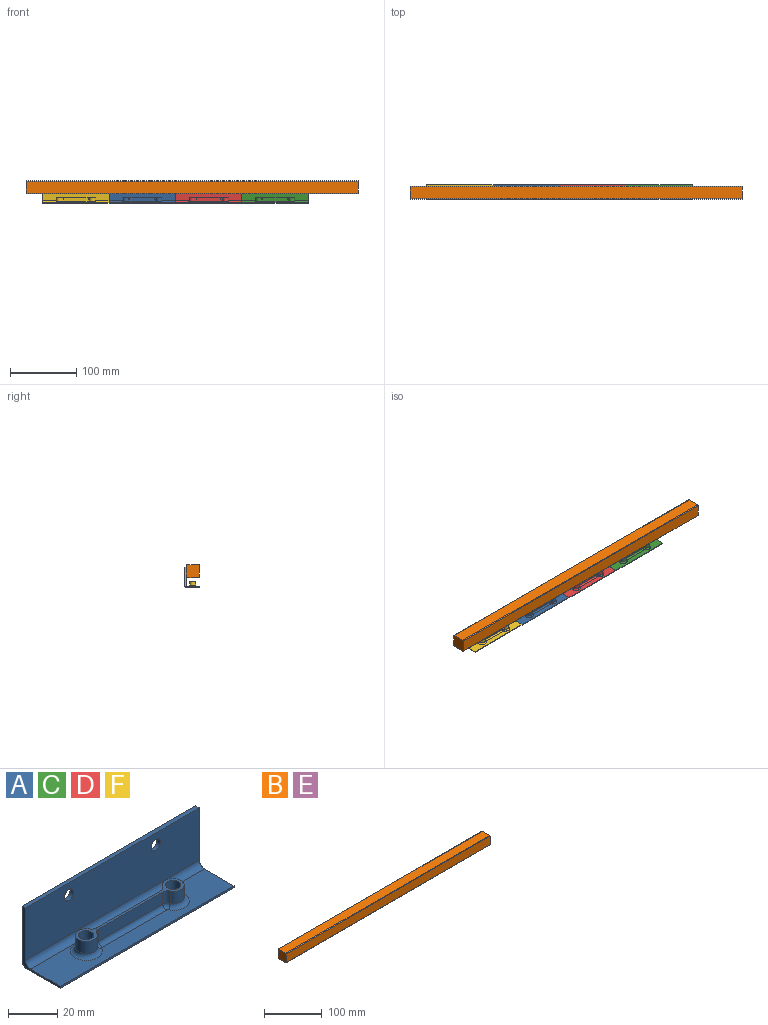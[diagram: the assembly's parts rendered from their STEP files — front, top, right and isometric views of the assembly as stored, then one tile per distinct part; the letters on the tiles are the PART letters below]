
ASSEMBLY  parts=6 mates=4
PART A: 35 faces, bbox 100x22x30 mm
  f0: plane 100x27mm, normal (0,1,0), area 2654.2mm2, adj f4,f5,f16,f20,f33,f34
  f1: plane 100x26mm, normal (0,-1,0), area 2554.2mm2, adj f4,f5,f16,f19,f33,f34
  f2: plane 100x19mm, normal (0,0,-1), area 1885.9mm2, adj f4,f5,f6,f17,f18,f20
  f3: plane 100x17mm, normal (0,0,1), area 1240mm2, adj f4,f5,f6,f19,f25,f26,f27,f28
  f4: plane 30x22mm, normal (1,0,0), area 80mm2, adj f0,f1,f2,f3,f6,f16,f19,f20
  f5: plane 30x22mm, normal (-1,0,0), area 80mm2, adj f0,f1,f2,f3,f6,f16,f19,f20
  f6: plane 100x1mm, normal (0,-1,0), area 100mm2, adj f2,f3,f4,f5
  f7: plane 36.84x6mm, normal (0,1,0), area 221mm2, adj f13,f22,f24,f28
  f8: cylinder r=4.5mm len=9mm, axis (0,0,-1), area 142.6mm2, adj f13,f21,f22,f25
  f9: plane 36.84x6mm, normal (0,-1,0), area 221mm2, adj f13,f21,f23,f29
  f10: cylinder r=3.1mm len=8mm, axis (0,0,-1), area 155.8mm2, adj f13,f14
  f11: cylinder r=4.5mm len=9mm, axis (0,0,-1), area 142.6mm2, adj f13,f23,f24,f32
  f12: cylinder r=3.1mm len=8mm, axis (0,0,-1), area 155.8mm2, adj f13,f15
  f13: plane 59x9mm, normal (0,0,1), area 118.9mm2, adj f7,f8,f9,f10,f11,f12,f21,f22
  f14: plane 6.2x6.2mm, normal (0,0,1), area 23.1mm2, adj f10,f17
  f15: plane 6.2x6.2mm, normal (0,0,1), area 23.1mm2, adj f12,f18
  f16: plane 100x2mm, normal (0,0,1), area 200mm2, adj f0,f1,f4,f5
  f17: cylinder r=1.5mm len=3mm, axis (0,0,1), area 9.4mm2, adj f2,f14
  f18: cylinder r=1.5mm len=3mm, axis (0,0,1), area 9.4mm2, adj f2,f15
  f19: cylinder r=3mm len=100mm, axis (-1,0,0), area 471.2mm2, adj f1,f3,f4,f5
  f20: cylinder r=3mm len=100mm, axis (-1,0,0), area 471.2mm2, adj f0,f2,f4,f5
  f21: cylinder r=3mm len=6mm, axis (0,0,-1), area 19.3mm2, adj f8,f9,f13,f27
  f22: cylinder r=3mm len=6mm, axis (0,0,-1), area 19.3mm2, adj f7,f8,f13,f26
  f23: cylinder r=3mm len=6mm, axis (0,0,-1), area 19.3mm2, adj f9,f11,f13,f31
  f24: cylinder r=3mm len=6mm, axis (0,0,-1), area 19.3mm2, adj f7,f11,f13,f30
  f25: torus R=6.5mm, axis (0,0,1), area 86.7mm2, adj f3,f8,f26,f27
  f26: torus R=1mm, axis (0,0,1), area 7.6mm2, adj f3,f22,f25,f28
  f27: torus R=1mm, axis (0,0,1), area 7.6mm2, adj f3,f21,f25,f29
  f28: cylinder r=2mm len=36.84mm, axis (-1,0,0), area 115.7mm2, adj f3,f7,f26,f30
  f29: cylinder r=2mm len=36.84mm, axis (1,0,0), area 115.7mm2, adj f3,f9,f27,f31
  f30: torus R=1mm, axis (0,0,1), area 7.6mm2, adj f3,f24,f28,f32
  f31: torus R=1mm, axis (0,0,1), area 7.6mm2, adj f3,f23,f29,f32
  f32: torus R=6.5mm, axis (0,0,1), area 86.7mm2, adj f3,f11,f30,f31
  f33: cylinder r=2.7mm len=5.4mm, axis (0,1,0), area 33.9mm2, adj f0,f1
  f34: cylinder r=2.7mm len=5.4mm, axis (0,1,0), area 33.9mm2, adj f0,f1
PART B: 10 faces, bbox 500x20x20 mm
  f0: plane 500x18mm, normal (0,-1,0), area 9000mm2, adj f1,f3,f7,f9
  f1: plane 20x20mm, normal (1,0,0), area 399.1mm2, adj f0,f2,f4,f5,f6,f7,f8,f9
  f2: plane 500x18mm, normal (0,1,0), area 9000mm2, adj f1,f3,f6,f8
  f3: plane 20x20mm, normal (-1,0,0), area 399.1mm2, adj f0,f2,f4,f5,f6,f7,f8,f9
  f4: plane 500x18mm, normal (0,0,1), area 9000mm2, adj f1,f3,f8,f9
  f5: plane 500x18mm, normal (0,0,-1), area 9000mm2, adj f1,f3,f6,f7
  f6: cylinder r=1mm len=500mm, axis (-1,0,0), area 785.4mm2, adj f1,f2,f3,f5
  f7: cylinder r=1mm len=500mm, axis (1,0,0), area 785.4mm2, adj f0,f1,f3,f5
  f8: cylinder r=1mm len=500mm, axis (1,0,0), area 785.4mm2, adj f1,f2,f3,f4
  f9: cylinder r=1mm len=500mm, axis (-1,0,0), area 785.4mm2, adj f0,f1,f3,f4
PART C: same geometry as A
PART D: same geometry as A
PART E: same geometry as B
PART F: same geometry as A
PLACE A t=(-179.93,-30.01,21.86)mm
PLACE B t=(-104.93,-30.01,35.86)mm
PLACE C t=(20.07,-30.01,21.86)mm
PLACE D t=(-79.93,-30.01,21.86)mm
PLACE E t=(-104.93,-30.01,35.86)mm
PLACE F t=(-279.93,-30.01,21.86)mm
MATE fastened F.f33 <-> E.f2  axis (0,-1,0) through (-254.93,-20.01,45.86)mm
MATE fastened C.f5 <-> D.f4  axis (-1,0,0) through (-29.93,-18.01,38.36)mm
MATE fastened A.f5 <-> F.f4  axis (-1,0,0) through (-229.93,-18.01,38.36)mm
MATE fastened D.f5 <-> A.f4  axis (-1,0,0) through (-129.93,-18.01,38.36)mm
